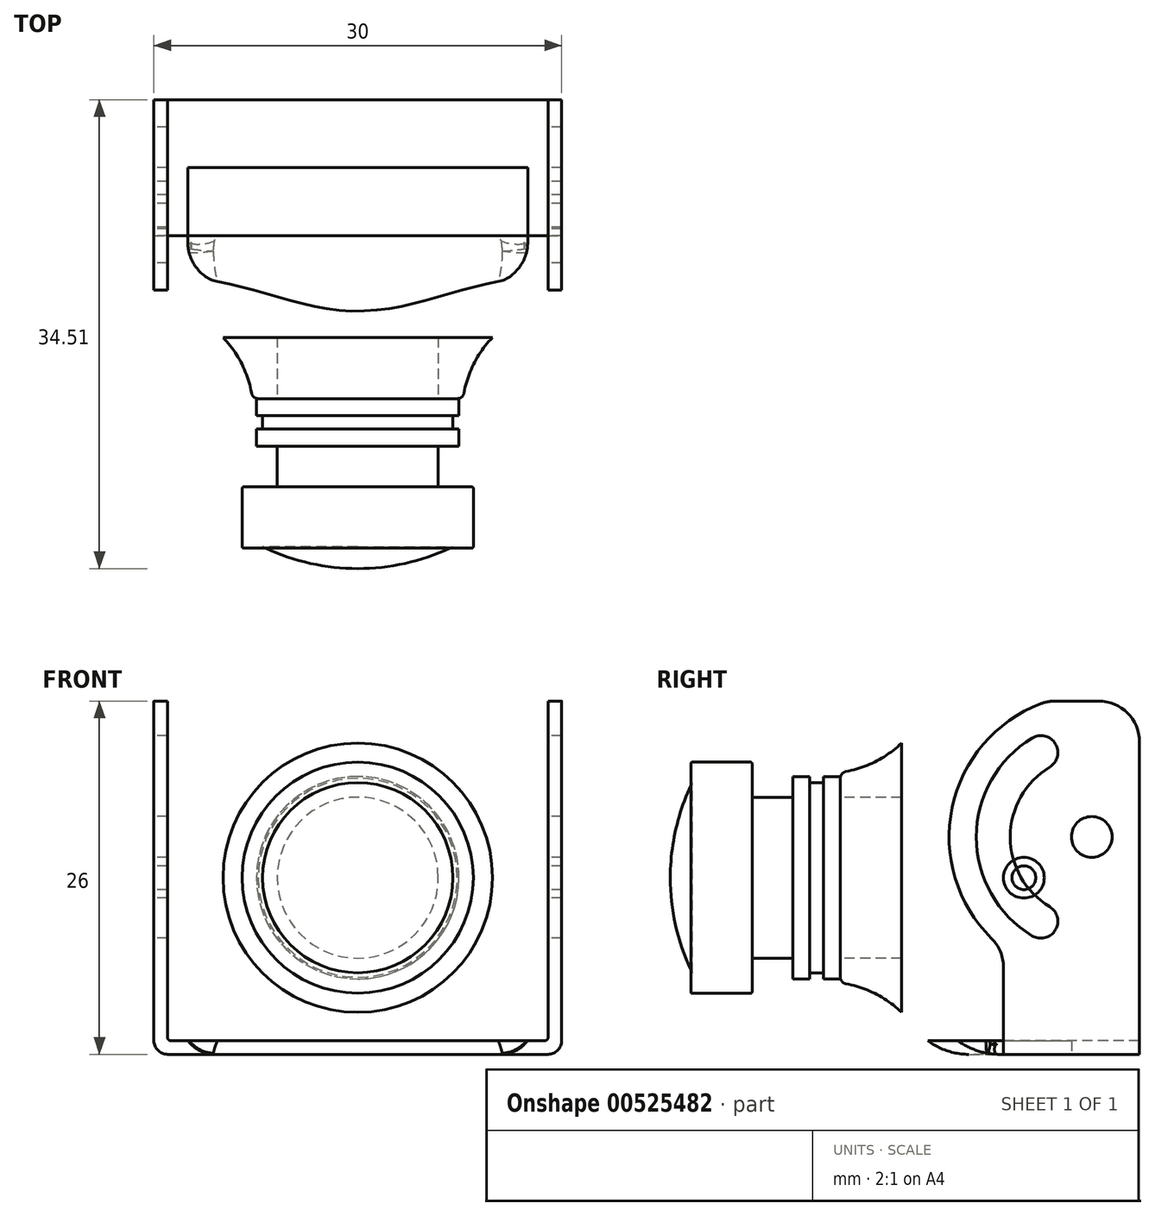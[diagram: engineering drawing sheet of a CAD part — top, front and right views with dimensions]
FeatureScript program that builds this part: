
annotation { "Feature Type Name" : "Feature", "Feature Type Description" : "" }
export const myFeature = defineFeature(function(context is Context, id is Id, definition is map)
    precondition{}
    {
        {
            var Q0;
            Q0=qCreatedBy(makeId("Right.planeOp"),FACE);
            var sketch = newSketch(context, id + "F0", { "sketchPlane" : qUnion([Q0])});
            skLineSegment(sketch, "E0", {"start": v(-18.38, 0) * mm, "end": v(-1.77, 16.62) * mm, "construction": true});
            skLineSegment(sketch, "E1", {"start": v(1.77, 16.62) * mm, "end": v(18.38, 0) * mm, "construction": true});
            skLineSegment(sketch, "E2", {"start": v(18.38, 0) * mm, "end": v(0, -18.38) * mm, "construction": true});
            skLineSegment(sketch, "E3", {"start": v(0, -18.38) * mm, "end": v(-18.38, 0) * mm, "construction": true});
            skArc(sketch, "E4", {"start": v(-5.5, 17.35) * mm, "mid": v(-8.56, 16.3) * mm, "end": v(-10.34, 13.6) * mm});
            skLineSegment(sketch, "E5", {"start": v(-17, 0) * mm, "end": v(-17, 7.32) * mm});
            skArc(sketch, "E6", {"start": v(-16.59, 7.81) * mm, "mid": v(-12.62, 9.8) * mm, "end": v(-10.34, 13.6) * mm});
            skLineSegment(sketch, "E7", {"start": v(0, 0) * mm, "end": v(-17, 0) * mm});
            skPoint(sketch, "E8.visualSharp", {"position": v(0, 18.38) * mm});
            skArc(sketch, "E8.filletArc", {"start": v(1.77, 16.62) * mm, "mid": v(0, 17.35) * mm, "end": v(-1.77, 16.62) * mm, "construction": true});
            skLineSegment(sketch, "E9", {"start": v(0, 17.35) * mm, "end": v(0, 0) * mm});
            skLineSegment(sketch, "E10", {"start": v(0, 17.35) * mm, "end": v(-5.5, 17.35) * mm});
            skPoint(sketch, "E11.visualSharp", {"position": v(-17, 7.75) * mm});
            skArc(sketch, "E11.filletArc", {"start": v(-16.59, 7.81) * mm, "mid": v(-16.88, 7.64) * mm, "end": v(-17, 7.32) * mm});
            skSolve(sketch);
        }
        {
            var Q0;
            Q0=qCreatedBy(makeId("Front.planeOp"),FACE);
            var sketch = newSketch(context, id + "F1", { "sketchPlane" : qUnion([Q0])});
            skLineSegment(sketch, "E12.bottom", {"start": v(10.5, 13) * mm, "end": v(-10.5, 13) * mm});
            skLineSegment(sketch, "E12.top", {"start": v(10.5, -13) * mm, "end": v(-10.5, -13) * mm});
            skLineSegment(sketch, "E12.left", {"start": v(13, 10.5) * mm, "end": v(13, -10.5) * mm});
            skLineSegment(sketch, "E12.right", {"start": v(-13, 10.5) * mm, "end": v(-13, -10.5) * mm});
            skPoint(sketch, "E13.visualSharp", {"position": v(13, 13) * mm});
            skArc(sketch, "E13.filletArc", {"start": v(13, 10.5) * mm, "mid": v(12.27, 12.27) * mm, "end": v(10.5, 13) * mm});
            skPoint(sketch, "E14.visualSharp", {"position": v(-13, 13) * mm});
            skArc(sketch, "E14.filletArc", {"start": v(-10.5, 13) * mm, "mid": v(-12.27, 12.27) * mm, "end": v(-13, 10.5) * mm});
            skPoint(sketch, "E15.visualSharp", {"position": v(13, -13) * mm});
            skArc(sketch, "E15.filletArc", {"start": v(10.5, -13) * mm, "mid": v(12.27, -12.27) * mm, "end": v(13, -10.5) * mm});
            skPoint(sketch, "E16.visualSharp", {"position": v(-13, -13) * mm});
            skArc(sketch, "E16.filletArc", {"start": v(-13, -10.5) * mm, "mid": v(-12.27, -12.27) * mm, "end": v(-10.5, -13) * mm});
            skLineSegment(sketch, "E17.bottom", {"start": v(20, 20) * mm, "end": v(-20, 20) * mm});
            skLineSegment(sketch, "E17.top", {"start": v(20, -20) * mm, "end": v(-20, -20) * mm});
            skLineSegment(sketch, "E17.left", {"start": v(20, 20) * mm, "end": v(20, -20) * mm});
            skLineSegment(sketch, "E17.right", {"start": v(-20, 20) * mm, "end": v(-20, -20) * mm});
            skSolve(sketch);
        }
        {
            var Q0;
            Q0=makeQuery(id+"F0.imprint","IMPRINT",FACE,{"disambiguationData":[TD([[makeQuery(id+"F0.imprint","IMPRINT",EDGE,{"derivedFrom":sQuery(id+"F0.wireOp",EDGE,"E4")}),1.0]])]});
            var Q1;
            Q1=sQuery(id+"F0.wireOp",EDGE,"E7");
            revolve(context, id + "F2", {"entities" : qUnion([Q0]), "axis" : qUnion([Q1]), "revolveType" : RevolveType.FULL});
        }
        {
            var Q0;
            Q0=qSketchRegion(id+"F1",true);
            extrude(context, id + "F3", {"entities" : qUnion([Q0]), "operationType" : NewBodyOperationType.REMOVE, "depth" : 25 * mm});
        }
        {
            var Q0;
            Q0=makeQuery(id+"F3.boolean.opBoolean","INTERSECT",EDGE,{"derivedFrom":[makeQuery(id+"F2.opRevolve","SWEPT_FACE",FACE,{"disambiguationData":[OSD([sQuery(id+"F0.wireOp",EDGE,"E6")])]}),makeQuery(id+"F3.opExtrude","SWEPT_FACE",FACE,{"disambiguationData":[OSD([sQuery(id+"F1.wireOp",EDGE,"E12.left")])]})]});
            var Q1;
            Q1=makeQuery(id+"F3.boolean.opBoolean","INTERSECT",EDGE,{"derivedFrom":[makeQuery(id+"F2.opRevolve","SWEPT_FACE",FACE,{"disambiguationData":[OSD([sQuery(id+"F0.wireOp",EDGE,"E6")])]}),makeQuery(id+"F3.opExtrude","SWEPT_FACE",FACE,{"disambiguationData":[OSD([sQuery(id+"F1.wireOp",EDGE,"E12.top")])]})]});
            var Q2;
            Q2=makeQuery(id+"F3.boolean.opBoolean","INTERSECT",EDGE,{"derivedFrom":[makeQuery(id+"F2.opRevolve","SWEPT_FACE",FACE,{"disambiguationData":[OSD([sQuery(id+"F0.wireOp",EDGE,"E6")])]}),makeQuery(id+"F3.opExtrude","SWEPT_FACE",FACE,{"disambiguationData":[OSD([sQuery(id+"F1.wireOp",EDGE,"E12.right")])]})]});
            var Q3;
            Q3=makeQuery(id+"F3.boolean.opBoolean","INTERSECT",EDGE,{"derivedFrom":[makeQuery(id+"F2.opRevolve","SWEPT_FACE",FACE,{"disambiguationData":[OSD([sQuery(id+"F0.wireOp",EDGE,"E6")])]}),makeQuery(id+"F3.opExtrude","SWEPT_FACE",FACE,{"disambiguationData":[OSD([sQuery(id+"F1.wireOp",EDGE,"E12.bottom")])]})]});
            fillet(context, id + "F4", {"entities" : qUnion([Q0, Q1, Q2, Q3]), "radius" : 5 * mm, "allowEdgeOverflow" : false});
        }
        {
            var Q0;
            {var subQ0=makeQuery(id+"F2.opRevolve","SWEPT_FACE",FACE,{"disambiguationData":[OSD([sQuery(id+"F0.wireOp",EDGE,"E6")])]});var subQ1=makeQuery(id+"F3.opExtrude","SWEPT_FACE",FACE,{"disambiguationData":[OSD([sQuery(id+"F1.wireOp",EDGE,"E12.top")])]});Q0=makeQuery(id+"F4.opFillet","BLEND_EDGE",EDGE,{"blendedFrom":[makeQuery(id+"F3.boolean.opBoolean","INTERSECT",EDGE,{"derivedFrom":[subQ0,subQ1]}),makeQuery(id+"F3.boolean.opBoolean","SPLIT",FACE,{"disambiguationData":[TD([makeQuery(id+"F3.opExtrude","SWEPT_FACE",FACE,{"disambiguationData":[OSD([sQuery(id+"F1.wireOp",EDGE,"E16.filletArc")])]})])],"derivedFrom":makeQuery(id+"F2.opRevolve","SWEPT_FACE",FACE,{"disambiguationData":[OSD([sQuery(id+"F0.wireOp",EDGE,"E4")])]})})],"blendedInto":[makeQuery(id+"F3.boolean.opBoolean","SPLIT",FACE,{"disambiguationData":[TD([makeQuery(id+"F3.opExtrude","SWEPT_FACE",FACE,{"disambiguationData":[OSD([sQuery(id+"F1.wireOp",EDGE,"E16.filletArc")])]})])],"derivedFrom":makeQuery(id+"F2.opRevolve","SWEPT_FACE",FACE,{"disambiguationData":[OSD([sQuery(id+"F0.wireOp",EDGE,"E4")])]})})]});}
            var Q1;
            {var subQ0=makeQuery(id+"F2.opRevolve","SWEPT_FACE",FACE,{"disambiguationData":[OSD([sQuery(id+"F0.wireOp",EDGE,"E6")])]});var subQ1=makeQuery(id+"F3.opExtrude","SWEPT_FACE",FACE,{"disambiguationData":[OSD([sQuery(id+"F1.wireOp",EDGE,"E12.right")])]});Q1=makeQuery(id+"F4.opFillet","BLEND_EDGE",EDGE,{"blendedFrom":[makeQuery(id+"F3.boolean.opBoolean","INTERSECT",EDGE,{"derivedFrom":[subQ0,subQ1]}),makeQuery(id+"F3.boolean.opBoolean","SPLIT",FACE,{"disambiguationData":[TD([makeQuery(id+"F3.opExtrude","SWEPT_FACE",FACE,{"disambiguationData":[OSD([sQuery(id+"F1.wireOp",EDGE,"E16.filletArc")])]})])],"derivedFrom":makeQuery(id+"F2.opRevolve","SWEPT_FACE",FACE,{"disambiguationData":[OSD([sQuery(id+"F0.wireOp",EDGE,"E4")])]})})],"blendedInto":[makeQuery(id+"F3.boolean.opBoolean","SPLIT",FACE,{"disambiguationData":[TD([makeQuery(id+"F3.opExtrude","SWEPT_FACE",FACE,{"disambiguationData":[OSD([sQuery(id+"F1.wireOp",EDGE,"E16.filletArc")])]})])],"derivedFrom":makeQuery(id+"F2.opRevolve","SWEPT_FACE",FACE,{"disambiguationData":[OSD([sQuery(id+"F0.wireOp",EDGE,"E4")])]})})]});}
            var Q2;
            {var subQ0=makeQuery(id+"F2.opRevolve","SWEPT_FACE",FACE,{"disambiguationData":[OSD([sQuery(id+"F0.wireOp",EDGE,"E6")])]});Q2=makeQuery(id+"F4.opFillet","BLEND_EDGE",EDGE,{"blendedFrom":[makeQuery(id+"F3.boolean.opBoolean","INTERSECT",EDGE,{"derivedFrom":[subQ0,makeQuery(id+"F3.opExtrude","SWEPT_FACE",FACE,{"disambiguationData":[OSD([sQuery(id+"F1.wireOp",EDGE,"E12.top")])]})]}),makeQuery(id+"F3.boolean.opBoolean","INTERSECT",EDGE,{"derivedFrom":[subQ0,makeQuery(id+"F3.opExtrude","SWEPT_FACE",FACE,{"disambiguationData":[OSD([sQuery(id+"F1.wireOp",EDGE,"E12.right")])]})]})],"blendedInto":[]});}
            var Q3;
            {var subQ0=makeQuery(id+"F2.opRevolve","SWEPT_FACE",FACE,{"disambiguationData":[OSD([sQuery(id+"F0.wireOp",EDGE,"E6")])]});Q3=makeQuery(id+"F4.opFillet","BLEND_EDGE",EDGE,{"blendedFrom":[makeQuery(id+"F3.boolean.opBoolean","INTERSECT",EDGE,{"derivedFrom":[subQ0,makeQuery(id+"F3.opExtrude","SWEPT_FACE",FACE,{"disambiguationData":[OSD([sQuery(id+"F1.wireOp",EDGE,"E12.bottom")])]})]}),makeQuery(id+"F3.boolean.opBoolean","INTERSECT",EDGE,{"derivedFrom":[subQ0,makeQuery(id+"F3.opExtrude","SWEPT_FACE",FACE,{"disambiguationData":[OSD([sQuery(id+"F1.wireOp",EDGE,"E12.right")])]})]})],"blendedInto":[]});}
            var Q4;
            {var subQ0=makeQuery(id+"F2.opRevolve","SWEPT_FACE",FACE,{"disambiguationData":[OSD([sQuery(id+"F0.wireOp",EDGE,"E6")])]});var subQ1=makeQuery(id+"F3.opExtrude","SWEPT_FACE",FACE,{"disambiguationData":[OSD([sQuery(id+"F1.wireOp",EDGE,"E12.right")])]});Q4=makeQuery(id+"F4.opFillet","BLEND_EDGE",EDGE,{"blendedFrom":[makeQuery(id+"F3.boolean.opBoolean","INTERSECT",EDGE,{"derivedFrom":[subQ0,subQ1]}),makeQuery(id+"F3.boolean.opBoolean","SPLIT",FACE,{"disambiguationData":[TD([makeQuery(id+"F3.opExtrude","SWEPT_FACE",FACE,{"disambiguationData":[OSD([sQuery(id+"F1.wireOp",EDGE,"E14.filletArc")])]})])],"derivedFrom":makeQuery(id+"F2.opRevolve","SWEPT_FACE",FACE,{"disambiguationData":[OSD([sQuery(id+"F0.wireOp",EDGE,"E4")])]})})],"blendedInto":[makeQuery(id+"F3.boolean.opBoolean","SPLIT",FACE,{"disambiguationData":[TD([makeQuery(id+"F3.opExtrude","SWEPT_FACE",FACE,{"disambiguationData":[OSD([sQuery(id+"F1.wireOp",EDGE,"E14.filletArc")])]})])],"derivedFrom":makeQuery(id+"F2.opRevolve","SWEPT_FACE",FACE,{"disambiguationData":[OSD([sQuery(id+"F0.wireOp",EDGE,"E4")])]})})]});}
            var Q5;
            {var subQ0=makeQuery(id+"F2.opRevolve","SWEPT_FACE",FACE,{"disambiguationData":[OSD([sQuery(id+"F0.wireOp",EDGE,"E6")])]});var subQ1=makeQuery(id+"F3.opExtrude","SWEPT_FACE",FACE,{"disambiguationData":[OSD([sQuery(id+"F1.wireOp",EDGE,"E12.bottom")])]});Q5=makeQuery(id+"F4.opFillet","BLEND_EDGE",EDGE,{"blendedFrom":[makeQuery(id+"F3.boolean.opBoolean","INTERSECT",EDGE,{"derivedFrom":[subQ0,subQ1]}),makeQuery(id+"F3.boolean.opBoolean","SPLIT",FACE,{"disambiguationData":[TD([makeQuery(id+"F3.opExtrude","SWEPT_FACE",FACE,{"disambiguationData":[OSD([sQuery(id+"F1.wireOp",EDGE,"E14.filletArc")])]})])],"derivedFrom":makeQuery(id+"F2.opRevolve","SWEPT_FACE",FACE,{"disambiguationData":[OSD([sQuery(id+"F0.wireOp",EDGE,"E4")])]})})],"blendedInto":[makeQuery(id+"F3.boolean.opBoolean","SPLIT",FACE,{"disambiguationData":[TD([makeQuery(id+"F3.opExtrude","SWEPT_FACE",FACE,{"disambiguationData":[OSD([sQuery(id+"F1.wireOp",EDGE,"E14.filletArc")])]})])],"derivedFrom":makeQuery(id+"F2.opRevolve","SWEPT_FACE",FACE,{"disambiguationData":[OSD([sQuery(id+"F0.wireOp",EDGE,"E4")])]})})]});}
            var Q6;
            {var subQ0=makeQuery(id+"F2.opRevolve","SWEPT_FACE",FACE,{"disambiguationData":[OSD([sQuery(id+"F0.wireOp",EDGE,"E6")])]});var subQ1=makeQuery(id+"F3.opExtrude","SWEPT_FACE",FACE,{"disambiguationData":[OSD([sQuery(id+"F1.wireOp",EDGE,"E12.bottom")])]});Q6=makeQuery(id+"F4.opFillet","BLEND_EDGE",EDGE,{"blendedFrom":[makeQuery(id+"F3.boolean.opBoolean","INTERSECT",EDGE,{"derivedFrom":[subQ0,subQ1]}),makeQuery(id+"F3.boolean.opBoolean","SPLIT",FACE,{"disambiguationData":[TD([makeQuery(id+"F3.opExtrude","SWEPT_FACE",FACE,{"disambiguationData":[OSD([sQuery(id+"F1.wireOp",EDGE,"E13.filletArc")])]})])],"derivedFrom":makeQuery(id+"F2.opRevolve","SWEPT_FACE",FACE,{"disambiguationData":[OSD([sQuery(id+"F0.wireOp",EDGE,"E4")])]})})],"blendedInto":[makeQuery(id+"F3.boolean.opBoolean","SPLIT",FACE,{"disambiguationData":[TD([makeQuery(id+"F3.opExtrude","SWEPT_FACE",FACE,{"disambiguationData":[OSD([sQuery(id+"F1.wireOp",EDGE,"E13.filletArc")])]})])],"derivedFrom":makeQuery(id+"F2.opRevolve","SWEPT_FACE",FACE,{"disambiguationData":[OSD([sQuery(id+"F0.wireOp",EDGE,"E4")])]})})]});}
            var Q7;
            {var subQ0=makeQuery(id+"F2.opRevolve","SWEPT_FACE",FACE,{"disambiguationData":[OSD([sQuery(id+"F0.wireOp",EDGE,"E6")])]});var subQ1=makeQuery(id+"F3.opExtrude","SWEPT_FACE",FACE,{"disambiguationData":[OSD([sQuery(id+"F1.wireOp",EDGE,"E12.left")])]});Q7=makeQuery(id+"F4.opFillet","BLEND_EDGE",EDGE,{"blendedFrom":[makeQuery(id+"F3.boolean.opBoolean","INTERSECT",EDGE,{"derivedFrom":[subQ0,subQ1]}),makeQuery(id+"F3.boolean.opBoolean","SPLIT",FACE,{"disambiguationData":[TD([makeQuery(id+"F3.opExtrude","SWEPT_FACE",FACE,{"disambiguationData":[OSD([sQuery(id+"F1.wireOp",EDGE,"E13.filletArc")])]})])],"derivedFrom":makeQuery(id+"F2.opRevolve","SWEPT_FACE",FACE,{"disambiguationData":[OSD([sQuery(id+"F0.wireOp",EDGE,"E4")])]})})],"blendedInto":[makeQuery(id+"F3.boolean.opBoolean","SPLIT",FACE,{"disambiguationData":[TD([makeQuery(id+"F3.opExtrude","SWEPT_FACE",FACE,{"disambiguationData":[OSD([sQuery(id+"F1.wireOp",EDGE,"E13.filletArc")])]})])],"derivedFrom":makeQuery(id+"F2.opRevolve","SWEPT_FACE",FACE,{"disambiguationData":[OSD([sQuery(id+"F0.wireOp",EDGE,"E4")])]})})]});}
            var Q8;
            {var subQ0=makeQuery(id+"F2.opRevolve","SWEPT_FACE",FACE,{"disambiguationData":[OSD([sQuery(id+"F0.wireOp",EDGE,"E6")])]});Q8=makeQuery(id+"F4.opFillet","BLEND_EDGE",EDGE,{"blendedFrom":[makeQuery(id+"F3.boolean.opBoolean","INTERSECT",EDGE,{"derivedFrom":[subQ0,makeQuery(id+"F3.opExtrude","SWEPT_FACE",FACE,{"disambiguationData":[OSD([sQuery(id+"F1.wireOp",EDGE,"E12.bottom")])]})]}),makeQuery(id+"F3.boolean.opBoolean","INTERSECT",EDGE,{"derivedFrom":[subQ0,makeQuery(id+"F3.opExtrude","SWEPT_FACE",FACE,{"disambiguationData":[OSD([sQuery(id+"F1.wireOp",EDGE,"E12.left")])]})]})],"blendedInto":[]});}
            var Q9;
            {var subQ0=makeQuery(id+"F2.opRevolve","SWEPT_FACE",FACE,{"disambiguationData":[OSD([sQuery(id+"F0.wireOp",EDGE,"E6")])]});var subQ1=makeQuery(id+"F3.opExtrude","SWEPT_FACE",FACE,{"disambiguationData":[OSD([sQuery(id+"F1.wireOp",EDGE,"E12.left")])]});Q9=makeQuery(id+"F4.opFillet","BLEND_EDGE",EDGE,{"blendedFrom":[makeQuery(id+"F3.boolean.opBoolean","INTERSECT",EDGE,{"derivedFrom":[subQ0,subQ1]}),makeQuery(id+"F3.boolean.opBoolean","SPLIT",FACE,{"disambiguationData":[TD([makeQuery(id+"F3.opExtrude","SWEPT_FACE",FACE,{"disambiguationData":[OSD([sQuery(id+"F1.wireOp",EDGE,"E15.filletArc")])]})])],"derivedFrom":makeQuery(id+"F2.opRevolve","SWEPT_FACE",FACE,{"disambiguationData":[OSD([sQuery(id+"F0.wireOp",EDGE,"E4")])]})})],"blendedInto":[makeQuery(id+"F3.boolean.opBoolean","SPLIT",FACE,{"disambiguationData":[TD([makeQuery(id+"F3.opExtrude","SWEPT_FACE",FACE,{"disambiguationData":[OSD([sQuery(id+"F1.wireOp",EDGE,"E15.filletArc")])]})])],"derivedFrom":makeQuery(id+"F2.opRevolve","SWEPT_FACE",FACE,{"disambiguationData":[OSD([sQuery(id+"F0.wireOp",EDGE,"E4")])]})})]});}
            var Q10;
            {var subQ0=makeQuery(id+"F2.opRevolve","SWEPT_FACE",FACE,{"disambiguationData":[OSD([sQuery(id+"F0.wireOp",EDGE,"E6")])]});var subQ1=makeQuery(id+"F3.opExtrude","SWEPT_FACE",FACE,{"disambiguationData":[OSD([sQuery(id+"F1.wireOp",EDGE,"E12.top")])]});Q10=makeQuery(id+"F4.opFillet","BLEND_EDGE",EDGE,{"blendedFrom":[makeQuery(id+"F3.boolean.opBoolean","INTERSECT",EDGE,{"derivedFrom":[subQ0,subQ1]}),makeQuery(id+"F3.boolean.opBoolean","SPLIT",FACE,{"disambiguationData":[TD([makeQuery(id+"F3.opExtrude","SWEPT_FACE",FACE,{"disambiguationData":[OSD([sQuery(id+"F1.wireOp",EDGE,"E15.filletArc")])]})])],"derivedFrom":makeQuery(id+"F2.opRevolve","SWEPT_FACE",FACE,{"disambiguationData":[OSD([sQuery(id+"F0.wireOp",EDGE,"E4")])]})})],"blendedInto":[makeQuery(id+"F3.boolean.opBoolean","SPLIT",FACE,{"disambiguationData":[TD([makeQuery(id+"F3.opExtrude","SWEPT_FACE",FACE,{"disambiguationData":[OSD([sQuery(id+"F1.wireOp",EDGE,"E15.filletArc")])]})])],"derivedFrom":makeQuery(id+"F2.opRevolve","SWEPT_FACE",FACE,{"disambiguationData":[OSD([sQuery(id+"F0.wireOp",EDGE,"E4")])]})})]});}
            var Q11;
            {var subQ0=makeQuery(id+"F2.opRevolve","SWEPT_FACE",FACE,{"disambiguationData":[OSD([sQuery(id+"F0.wireOp",EDGE,"E6")])]});Q11=makeQuery(id+"F4.opFillet","BLEND_EDGE",EDGE,{"blendedFrom":[makeQuery(id+"F3.boolean.opBoolean","INTERSECT",EDGE,{"derivedFrom":[subQ0,makeQuery(id+"F3.opExtrude","SWEPT_FACE",FACE,{"disambiguationData":[OSD([sQuery(id+"F1.wireOp",EDGE,"E12.top")])]})]}),makeQuery(id+"F3.boolean.opBoolean","INTERSECT",EDGE,{"derivedFrom":[subQ0,makeQuery(id+"F3.opExtrude","SWEPT_FACE",FACE,{"disambiguationData":[OSD([sQuery(id+"F1.wireOp",EDGE,"E12.left")])]})]})],"blendedInto":[]});}
            fillet(context, id + "F5", {"entities" : qUnion([Q0, Q1, Q2, Q3, Q4, Q5, Q6, Q7, Q8, Q9, Q10, Q11]), "radius" : 2.4 * mm, "allowEdgeOverflow" : false});
        }
        {
            var Q0;
            Q0=makeQuery(id+"F2.opRevolve","SWEPT_FACE",FACE,{"disambiguationData":[OSD([sQuery(id+"F0.wireOp",EDGE,"E9")])]});
            var sketch = newSketch(context, id + "F6", { "sketchPlane" : qUnion([Q0])});
            skLineSegment(sketch, "E18.bottom", {"start": v(-10.5, 12) * mm, "end": v(10.5, 12) * mm});
            skLineSegment(sketch, "E18.top", {"start": v(-10.5, -12) * mm, "end": v(1, -12) * mm});
            skLineSegment(sketch, "E18.left", {"start": v(-12, 10.5) * mm, "end": v(-12, -10.5) * mm});
            skLineSegment(sketch, "E18.right", {"start": v(12, 10.5) * mm, "end": v(12, -8) * mm});
            skPoint(sketch, "E19.visualSharp", {"position": v(-12, 12) * mm});
            skArc(sketch, "E19.filletArc", {"start": v(-10.5, 12) * mm, "mid": v(-11.56, 11.56) * mm, "end": v(-12, 10.5) * mm});
            skPoint(sketch, "E20.visualSharp", {"position": v(-12, -12) * mm});
            skArc(sketch, "E20.filletArc", {"start": v(-12, -10.5) * mm, "mid": v(-11.56, -11.56) * mm, "end": v(-10.5, -12) * mm});
            skPoint(sketch, "E21.visualSharp", {"position": v(12, 12) * mm});
            skArc(sketch, "E21.filletArc", {"start": v(12, 10.5) * mm, "mid": v(11.56, 11.56) * mm, "end": v(10.5, 12) * mm});
            skPoint(sketch, "E22.visualSharp", {"position": v(12, -12) * mm});
            skLineSegment(sketch, "E23", {"start": v(1, -12) * mm, "end": v(1, -8) * mm});
            skLineSegment(sketch, "E24", {"start": v(1, -8) * mm, "end": v(12, -8) * mm});
            skCircle(sketch, "E25", {"center": v(-10, -10) * mm, "radius": 1.4 * mm});
            skCircle(sketch, "E26", {"center": v(10, 10) * mm, "radius": 1.4 * mm});
            skSolve(sketch);
        }
        {
            var Q0;
            Q0=makeQuery(id+"F6.imprint","IMPRINT",FACE,{"disambiguationData":[TD([[makeQuery(id+"F6.imprint","IMPRINT",EDGE,{"derivedFrom":sQuery(id+"F6.wireOp",EDGE,"E18.bottom")}),-1.0]])]});
            var Q1;
            Q1=makeQuery(id+"F6.imprint","IMPRINT",FACE,{"disambiguationData":[TD([[makeQuery(id+"F6.imprint","IMPRINT",EDGE,{"derivedFrom":sQuery(id+"F6.wireOp",EDGE,"E26")}),1.0]])]});
            var Q2;
            Q2=makeQuery(id+"F6.imprint","IMPRINT",FACE,{"disambiguationData":[TD([[makeQuery(id+"F6.imprint","IMPRINT",EDGE,{"derivedFrom":sQuery(id+"F6.wireOp",EDGE,"E25")}),1.0]])]});
            extrude(context, id + "F7", {"entities" : qUnion([Q0, Q1, Q2]), "operationType" : NewBodyOperationType.REMOVE, "oppositeDirection" : true, "depth" : 0.1 * mm});
        }
        {
            var Q0;
            Q0=makeQuery(id+"F6.imprint","IMPRINT",FACE,{"disambiguationData":[TD([[makeQuery(id+"F6.imprint","IMPRINT",EDGE,{"derivedFrom":sQuery(id+"F6.wireOp",EDGE,"E26")}),1.0]])]});
            var Q1;
            Q1=makeQuery(id+"F6.imprint","IMPRINT",FACE,{"disambiguationData":[TD([[makeQuery(id+"F6.imprint","IMPRINT",EDGE,{"derivedFrom":sQuery(id+"F6.wireOp",EDGE,"E25")}),1.0]])]});
            extrude(context, id + "F8", {"entities" : qUnion([Q0, Q1]), "operationType" : NewBodyOperationType.REMOVE, "oppositeDirection" : true, "depth" : 0.3 * mm});
        }
        {
            var Q0;
            Q0=makeQuery(id+"F8.boolean.opBoolean","INTERSECT",EDGE,{"derivedFrom":[makeQuery(id+"F7.boolean.opBoolean","COPY",FACE,{"derivedFrom":makeQuery(id+"F7.opExtrude","CAP_FACE",FACE,{"disambiguationData":[OSD([sQuery(id+"F6.wireOp",EDGE,"E18.bottom"),sQuery(id+"F6.wireOp",EDGE,"E18.top"),sQuery(id+"F6.wireOp",EDGE,"E18.left"),sQuery(id+"F6.wireOp",EDGE,"E18.right"),sQuery(id+"F6.wireOp",EDGE,"E19.filletArc"),sQuery(id+"F6.wireOp",EDGE,"E20.filletArc"),sQuery(id+"F6.wireOp",EDGE,"E21.filletArc"),sQuery(id+"F6.wireOp",EDGE,"E23"),sQuery(id+"F6.wireOp",EDGE,"E24")])],"isStart":false})}),makeQuery(id+"F8.opExtrude","SWEPT_FACE",FACE,{"disambiguationData":[OSD([sQuery(id+"F6.wireOp",EDGE,"E26")])]})]});
            var Q1;
            Q1=makeQuery(id+"F8.boolean.opBoolean","INTERSECT",EDGE,{"derivedFrom":[makeQuery(id+"F7.boolean.opBoolean","COPY",FACE,{"derivedFrom":makeQuery(id+"F7.opExtrude","CAP_FACE",FACE,{"disambiguationData":[OSD([sQuery(id+"F6.wireOp",EDGE,"E18.bottom"),sQuery(id+"F6.wireOp",EDGE,"E18.top"),sQuery(id+"F6.wireOp",EDGE,"E18.left"),sQuery(id+"F6.wireOp",EDGE,"E18.right"),sQuery(id+"F6.wireOp",EDGE,"E19.filletArc"),sQuery(id+"F6.wireOp",EDGE,"E20.filletArc"),sQuery(id+"F6.wireOp",EDGE,"E21.filletArc"),sQuery(id+"F6.wireOp",EDGE,"E23"),sQuery(id+"F6.wireOp",EDGE,"E24")])],"isStart":false})}),makeQuery(id+"F8.opExtrude","SWEPT_FACE",FACE,{"disambiguationData":[OSD([sQuery(id+"F6.wireOp",EDGE,"E25")])]})]});
            chamfer(context, id + "F9", {"entities" : qUnion([Q0, Q1]), "width" : 0.1 * mm, "tangentPropagation" : true});
        }
        {
            var Q0;
            Q0=makeQuery(id+"F2.opRevolve","SWEPT_FACE",FACE,{"disambiguationData":[OSD([sQuery(id+"F0.wireOp",EDGE,"E9")])]});
            var sketch = newSketch(context, id + "F10", { "sketchPlane" : qUnion([Q0])});
            skLineSegment(sketch, "E27.bottom", {"start": v(1, -8) * mm, "end": v(10.9, -8) * mm});
            skLineSegment(sketch, "E27.top", {"start": v(1, -11.3) * mm, "end": v(10.9, -11.3) * mm});
            skLineSegment(sketch, "E27.left", {"start": v(1, -8) * mm, "end": v(1, -11.3) * mm});
            skLineSegment(sketch, "E27.right", {"start": v(10.9, -8) * mm, "end": v(10.9, -11.3) * mm});
            skSolve(sketch);
        }
        {
            var Q0;
            Q0=qSketchRegion(id+"F10",true);
            extrude(context, id + "F11", {"entities" : qUnion([Q0]), "operationType" : NewBodyOperationType.ADD, "depth" : 1.6 * mm});
        }
        {
            var Q0;
            Q0=makeQuery(id+"F2.opRevolve","SWEPT_FACE",FACE,{"disambiguationData":[OSD([sQuery(id+"F0.wireOp",EDGE,"E5")])]});
            var sketch = newSketch(context, id + "F12", { "sketchPlane" : qUnion([Q0])});
            skCircle(sketch, "E28", {"center": v(0, 0) * mm, "radius": 5.92 * mm});
            skSolve(sketch);
        }
        {
            var Q0;
            Q0=makeQuery(id+"F12.imprint","IMPRINT",FACE,{"disambiguationData":[TD([[makeQuery(id+"F12.imprint","IMPRINT",EDGE,{"derivedFrom":sQuery(id+"F12.wireOp",EDGE,"E28")}),1.0]])]});
            extrude(context, id + "F13", {"entities" : qUnion([Q0]), "operationType" : NewBodyOperationType.REMOVE, "oppositeDirection" : true, "depth" : 12 * mm});
        }
        {
            var Q0;
            Q0=qCreatedBy(makeId("Right.planeOp"),FACE);
            var sketch = newSketch(context, id + "F14", { "sketchPlane" : qUnion([Q0])});
            skArc(sketch, "E29", {"start": v(-3.6, 2.5) * mm, "mid": v(-6, 0) * mm, "end": v(-3.6, -2.5) * mm});
            skLineSegment(sketch, "E30", {"start": v(-3.6, 2.5) * mm, "end": v(0, 2.65) * mm});
            skLineSegment(sketch, "E31", {"start": v(-3.6, -2.5) * mm, "end": v(0, -2.65) * mm});
            skLineSegment(sketch, "E32", {"start": v(0, -2.65) * mm, "end": v(0, 2.65) * mm});
            skSolve(sketch);
        }
        {
            var Q0;
            Q0=qSketchRegion(id+"F14",true);
            extrude(context, id + "F15", {"entities" : qUnion([Q0]), "operationType" : NewBodyOperationType.ADD, "endBound" : BoundingType.SYMMETRIC, "depth" : 26.25 * mm});
        }
        {
            var Q0;
            Q0=qCreatedBy(makeId("Right.planeOp"),FACE);
            var sketch = newSketch(context, id + "F16", { "sketchPlane" : qUnion([Q0])});
            skCircle(sketch, "E33", {"center": v(-3.5, 0) * mm, "radius": 2 * mm});
            skSolve(sketch);
        }
        {
            var Q0;
            Q0=qSketchRegion(id+"F16",true);
            extrude(context, id + "F17", {"entities" : qUnion([Q0]), "operationType" : NewBodyOperationType.ADD, "endBound" : BoundingType.SYMMETRIC, "depth" : 28 * mm});
        }
        {
            var Q0;
            Q0=qCreatedBy(makeId("Right.planeOp"),FACE);
            var sketch = newSketch(context, id + "F18", { "sketchPlane" : qUnion([Q0])});
            skCircle(sketch, "E34", {"center": v(-3.5, 0) * mm, "radius": 1.5 * mm});
            skCircle(sketch, "E35", {"center": v(-3.5, 0) * mm, "radius": 0.88 * mm});
            skSolve(sketch);
        }
        {
            var Q0;
            Q0=qSketchRegion(id+"F18",true);
            extrude(context, id + "F19", {"entities" : qUnion([Q0]), "operationType" : NewBodyOperationType.ADD, "endBound" : BoundingType.SYMMETRIC, "depth" : 30 * mm});
        }
        {
            var Q0;
            Q0=makeQuery(id+"F15.boolean.opBoolean","MERGE",FACE,{"derivedFrom":[makeQuery(id+"F2.opRevolve","SWEPT_FACE",FACE,{"disambiguationData":[OSD([sQuery(id+"F0.wireOp",EDGE,"E9")])]}),makeQuery(id+"F15.opExtrude","SWEPT_FACE",FACE,{"disambiguationData":[OSD([sQuery(id+"F14.wireOp",EDGE,"E32")])]})]});
            var sketch = newSketch(context, id + "F20", { "sketchPlane" : qUnion([Q0])});
            skLineSegment(sketch, "E36.bottom", {"start": v(-12, 2.65) * mm, "end": v(12, 2.65) * mm});
            skLineSegment(sketch, "E36.top", {"start": v(-12, -2.65) * mm, "end": v(12, -2.65) * mm});
            skLineSegment(sketch, "E36.left", {"start": v(-12, 2.65) * mm, "end": v(-12, -2.65) * mm});
            skLineSegment(sketch, "E36.right", {"start": v(12, 2.65) * mm, "end": v(12, -2.65) * mm});
            skSolve(sketch);
        }
        {
            var Q0;
            Q0=makeQuery(id+"F20.imprint","IMPRINT",FACE,{"disambiguationData":[TD([[makeQuery(id+"F20.imprint","IMPRINT",EDGE,{"derivedFrom":sQuery(id+"F20.wireOp",EDGE,"E36.bottom")}),-1.0]])]});
            extrude(context, id + "F21", {"entities" : qUnion([Q0]), "operationType" : NewBodyOperationType.REMOVE, "oppositeDirection" : true, "depth" : 0.1 * mm});
        }
        {
            var Q0;
            Q0=makeQuery(id+"F2.opRevolve","SWEPT_FACE",FACE,{"disambiguationData":[OSD([sQuery(id+"F0.wireOp",EDGE,"E5")])]});
            var sketch = newSketch(context, id + "F22", { "sketchPlane" : qUnion([Q0])});
            skCircle(sketch, "E37", {"center": v(0, 0) * mm, "radius": 7.45 * mm});
            skSolve(sketch);
        }
        {
            var Q0;
            Q0=qSketchRegion(id+"F22",true);
            extrude(context, id + "F23", {"entities" : qUnion([Q0]), "operationType" : NewBodyOperationType.ADD, "depth" : 3.5 * mm});
        }
        {
            var Q0;
            Q0=makeQuery(id+"F23.opExtrude","CAP_FACE",FACE,{"disambiguationData":[OSD([sQuery(id+"F22.wireOp",EDGE,"E37")])],"isStart":false});
            var sketch = newSketch(context, id + "F24", { "sketchPlane" : qUnion([Q0])});
            skCircle(sketch, "E38", {"center": v(0, 0) * mm, "radius": 5.92 * mm});
            skSolve(sketch);
        }
        {
            var Q0;
            Q0=makeQuery(id+"F24.imprint","IMPRINT",FACE,{"disambiguationData":[TD([[makeQuery(id+"F24.imprint","IMPRINT",EDGE,{"derivedFrom":sQuery(id+"F24.wireOp",EDGE,"E38")}),1.0]])]});
            extrude(context, id + "F25", {"entities" : qUnion([Q0]), "operationType" : NewBodyOperationType.ADD, "depth" : 3 * mm});
        }
        {
            var Q0;
            Q0=makeQuery(id+"F25.opExtrude","CAP_FACE",FACE,{"disambiguationData":[OSD([sQuery(id+"F24.wireOp",EDGE,"E38")])],"isStart":false});
            var sketch = newSketch(context, id + "F26", { "sketchPlane" : qUnion([Q0])});
            skCircle(sketch, "E39", {"center": v(0, 0) * mm, "radius": 8.5 * mm});
            skSolve(sketch);
        }
        {
            var Q0;
            Q0=qSketchRegion(id+"F26",true);
            extrude(context, id + "F27", {"entities" : qUnion([Q0]), "operationType" : NewBodyOperationType.ADD, "depth" : 4.5 * mm});
        }
        {
            var Q0;
            Q0=makeQuery(id+"F27.opExtrude","CAP_FACE",FACE,{"disambiguationData":[OSD([sQuery(id+"F26.wireOp",EDGE,"E39")])],"isStart":false});
            var sketch = newSketch(context, id + "F28", { "sketchPlane" : qUnion([Q0])});
            skCircle(sketch, "E40", {"center": v(0, 0) * mm, "radius": 7 * mm});
            skSolve(sketch);
        }
        {
            var Q0;
            Q0=makeQuery(id+"F28.imprint","IMPRINT",FACE,{"disambiguationData":[TD([[makeQuery(id+"F28.imprint","IMPRINT",EDGE,{"derivedFrom":sQuery(id+"F28.wireOp",EDGE,"E40")}),1.0]])]});
            extrude(context, id + "F29", {"entities" : qUnion([Q0]), "operationType" : NewBodyOperationType.REMOVE, "oppositeDirection" : true, "depth" : 0.1 * mm});
        }
        {
            var Q0;
            Q0=qCreatedBy(makeId("Right.planeOp"),FACE);
            var sketch = newSketch(context, id + "F30", { "sketchPlane" : qUnion([Q0])});
            skLineSegment(sketch, "E41", {"start": v(-27.9, 0) * mm, "end": v(-27.9, 7) * mm});
            skArc(sketch, "E42", {"start": v(-27.9, 7) * mm, "mid": v(-29.1, 3.6) * mm, "end": v(-29.51, 0) * mm});
            skLineSegment(sketch, "E43", {"start": v(-27.9, 0) * mm, "end": v(-29.51, 0) * mm});
            skPoint(sketch, "E44.orphan", {"position": v(-27.9, -7) * mm});
            skSolve(sketch);
        }
        {
            var Q0;
            Q0=qSketchRegion(id+"F30",true);
            var Q1;
            Q1=sQuery(id+"F30.wireOp",EDGE,"E43");
            revolve(context, id + "F31", {"operationType" : NewBodyOperationType.ADD, "entities" : qUnion([Q0]), "axis" : qUnion([Q1]), "revolveType" : RevolveType.FULL});
        }
        {
            var Q0;
            Q0=qCreatedBy(makeId("Right.planeOp"),FACE);
            var sketch = newSketch(context, id + "F32", { "sketchPlane" : qUnion([Q0])});
            skLineSegment(sketch, "E45.bottom", {"start": v(-19.25, 7.5) * mm, "end": v(-18.25, 7.5) * mm});
            skLineSegment(sketch, "E45.top", {"start": v(-19.25, 7) * mm, "end": v(-18.25, 7) * mm});
            skLineSegment(sketch, "E45.left", {"start": v(-19.25, 7.5) * mm, "end": v(-19.25, 7) * mm});
            skLineSegment(sketch, "E45.right", {"start": v(-18.25, 7.5) * mm, "end": v(-18.25, 7) * mm});
            skSolve(sketch);
        }
        {
            var Q0;
            Q0=qSketchRegion(id+"F32",true);
            var Q1;
            Q1=sQuery(id+"F30.wireOp",EDGE,"E43");
            revolve(context, id + "F33", {"operationType" : NewBodyOperationType.REMOVE, "entities" : qUnion([Q0]), "axis" : qUnion([Q1]), "revolveType" : RevolveType.FULL, "oppositeDirection" : true});
        }
        {
            var Q0;
            Q0=makeQuery(id+"F27.opExtrude","CAP_EDGE",EDGE,{"disambiguationData":[OSD([sQuery(id+"F26.wireOp",EDGE,"E39")])],"isStart":false});
            var Q1;
            Q1=makeQuery(id+"F27.opExtrude","CAP_EDGE",EDGE,{"disambiguationData":[OSD([sQuery(id+"F26.wireOp",EDGE,"E39")])],"isStart":true});
            fillet(context, id + "F34", {"entities" : qUnion([Q0, Q1]), "radius" : 0.1 * mm, "tangentPropagation" : true, "allowEdgeOverflow" : false});
        }
        {
            var Q0;
            Q0=qCreatedBy(makeId("Right.planeOp"),FACE);
            var sketch = newSketch(context, id + "F35", { "sketchPlane" : qUnion([Q0])});
            skLineSegment(sketch, "E46.bottom", {"start": v(5, -13) * mm, "end": v(-5, -13) * mm});
            skLineSegment(sketch, "E46.top", {"start": v(2, 13) * mm, "end": v(-1.2, 13) * mm});
            skLineSegment(sketch, "E46.left", {"start": v(5, -13) * mm, "end": v(5, 10) * mm});
            skLineSegment(sketch, "E46.right", {"start": v(-5, -13) * mm, "end": v(-5, -6.6) * mm});
            skCircle(sketch, "E47", {"center": v(1.5, 3) * mm, "radius": 1.5 * mm});
            skArc(sketch, "E48", {"start": v(-1.6, 8.14) * mm, "mid": v(-4.5, 3) * mm, "end": v(-1.6, -2.14) * mm});
            skArc(sketch, "E49", {"start": v(-2.9, 10.27) * mm, "mid": v(-7, 3) * mm, "end": v(-2.9, -4.27) * mm});
            skArc(sketch, "E50", {"start": v(-2.27, 12.8) * mm, "mid": v(-8.78, 5.15) * mm, "end": v(-5.89, -4.46) * mm});
            skCircle(sketch, "E51", {"center": v(1.5, 3) * mm, "radius": 7.25 * mm, "construction": true});
            skArc(sketch, "E52", {"start": v(-1.6, 8.14) * mm, "mid": v(-1.18, 9.85) * mm, "end": v(-2.9, 10.27) * mm});
            skArc(sketch, "E53", {"start": v(-2.9, -4.27) * mm, "mid": v(-1.18, -3.85) * mm, "end": v(-1.6, -2.14) * mm});
            skPoint(sketch, "E54.visualSharp", {"position": v(5, 13) * mm});
            skArc(sketch, "E54.filletArc", {"start": v(5, 10) * mm, "mid": v(4.12, 12.12) * mm, "end": v(2, 13) * mm});
            skPoint(sketch, "E55.visualSharp", {"position": v(-1.7, 13) * mm});
            skArc(sketch, "E55.filletArc", {"start": v(-1.2, 13) * mm, "mid": v(-1.74, 12.95) * mm, "end": v(-2.27, 12.8) * mm});
            skPoint(sketch, "E56.visualSharp", {"position": v(-5, -5.25) * mm});
            skArc(sketch, "E56.filletArc", {"start": v(-5, -6.6) * mm, "mid": v(-5.23, -5.44) * mm, "end": v(-5.89, -4.46) * mm});
            skSolve(sketch);
        }
        {
            var Q0;
            Q0=qSketchRegion(id+"F35",true);
            extrude(context, id + "F36", {"entities" : qUnion([Q0]), "endBound" : BoundingType.SYMMETRIC, "depth" : 30 * mm, "offsetDistance" : 25 * mm});
        }
        {
            var Q0;
            Q0=makeQuery(id+"F36.opExtrude","CAP_EDGE",EDGE,{"disambiguationData":[OSD([sQuery(id+"F35.wireOp",EDGE,"E46.bottom")])],"isStart":false});
            var Q1;
            Q1=makeQuery(id+"F36.opExtrude","CAP_EDGE",EDGE,{"disambiguationData":[OSD([sQuery(id+"F35.wireOp",EDGE,"E46.bottom")])],"isStart":true});
            fillet(context, id + "F37", {"entities" : qUnion([Q0, Q1]), "radius" : 1 * mm, "tangentPropagation" : true, "allowEdgeOverflow" : false});
        }
        {
            var Q0;
            Q0=qCreatedBy(makeId("Front.planeOp"),FACE);
            var sketch = newSketch(context, id + "F38", { "sketchPlane" : qUnion([Q0])});
            skLineSegment(sketch, "E57.bottom", {"start": v(14, 13) * mm, "end": v(-14, 13) * mm});
            skLineSegment(sketch, "E57.top", {"start": v(14, -12) * mm, "end": v(-14, -12) * mm});
            skLineSegment(sketch, "E57.left", {"start": v(14, 13) * mm, "end": v(14, -12) * mm});
            skLineSegment(sketch, "E57.right", {"start": v(-14, 13) * mm, "end": v(-14, -12) * mm});
            skSolve(sketch);
        }
        {
            var Q0;
            Q0=qSketchRegion(id+"F38",true);
            extrude(context, id + "F39", {"entities" : qUnion([Q0]), "operationType" : NewBodyOperationType.REMOVE, "endBound" : BoundingType.SYMMETRIC, "oppositeDirection" : true, "depth" : 25 * mm, "offsetDistance" : 25 * mm});
        }
        {
            var Q0;
            Q0=makeQuery(id+"F39.boolean.opBoolean","COPY",EDGE,{"derivedFrom":makeQuery(id+"F39.opExtrude","SWEPT_EDGE",EDGE,{"disambiguationData":[OSD([sQuery(id+"F38.wireOp",EDGE,"E57.top"),sQuery(id+"F38.wireOp",EDGE,"E57.right")])]})});
            var Q1;
            Q1=makeQuery(id+"F39.boolean.opBoolean","COPY",EDGE,{"derivedFrom":makeQuery(id+"F39.opExtrude","SWEPT_EDGE",EDGE,{"disambiguationData":[OSD([sQuery(id+"F38.wireOp",EDGE,"E57.top"),sQuery(id+"F38.wireOp",EDGE,"E57.left")])]})});
            fillet(context, id + "F40", {"entities" : qUnion([Q0, Q1]), "radius" : 0.25 * mm, "tangentPropagation" : true, "allowEdgeOverflow" : false});
        }
    });
